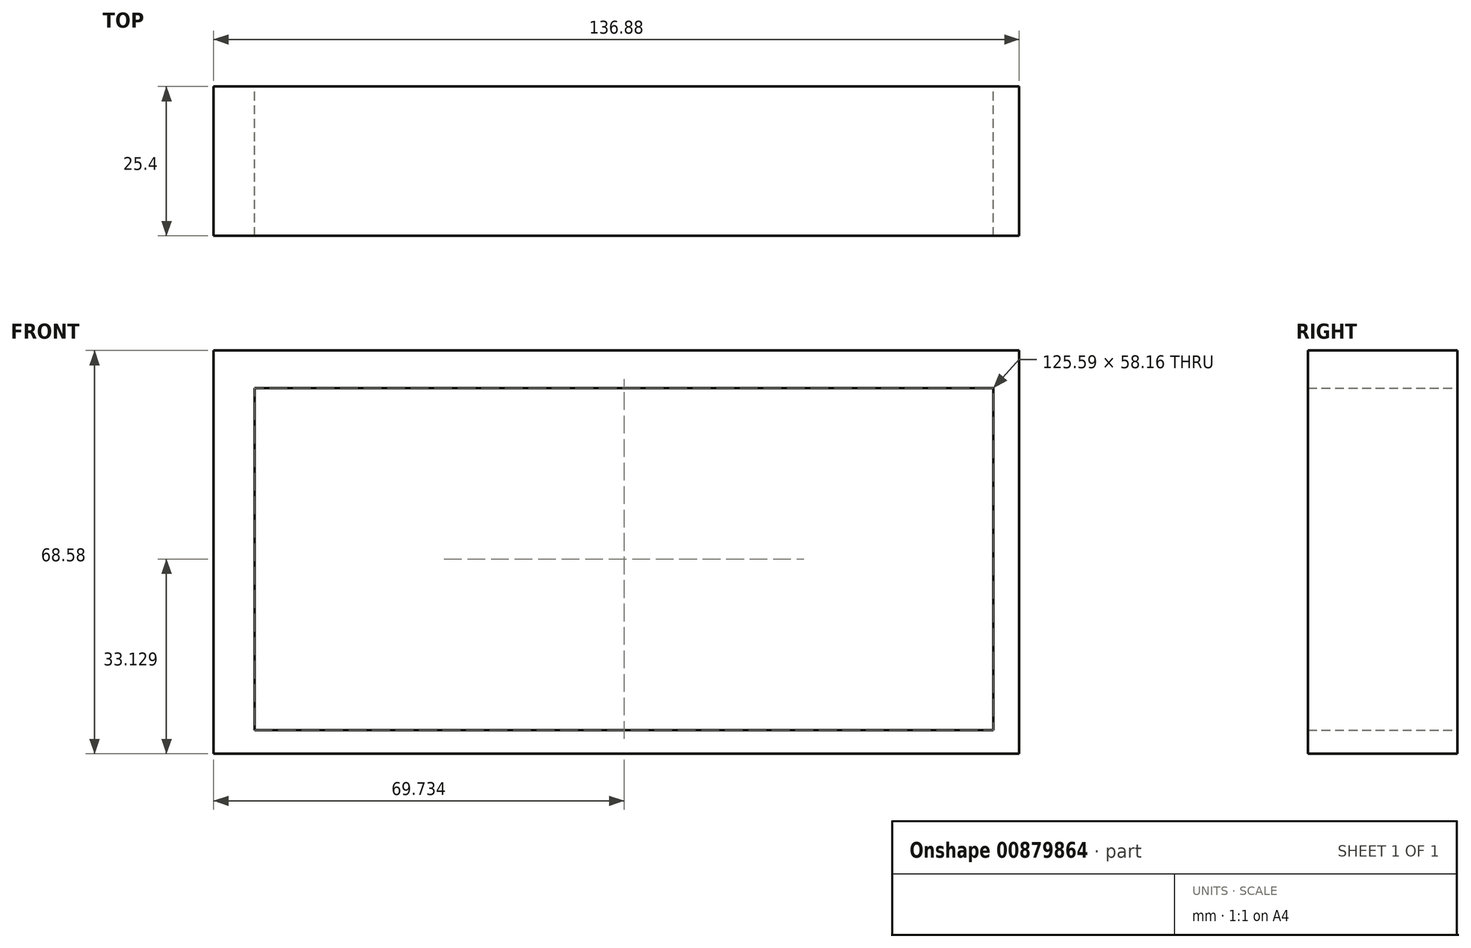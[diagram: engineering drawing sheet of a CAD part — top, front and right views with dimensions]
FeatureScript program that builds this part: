
annotation { "Feature Type Name" : "Feature", "Feature Type Description" : "" }
export const myFeature = defineFeature(function(context is Context, id is Id, definition is map)
    precondition{}
    {
        {
            var Q0;
            Q0=qCreatedBy(makeId("Front.planeOp"),FACE);
            var sketch = newSketch(context, id + "F0", { "sketchPlane" : qUnion([Q0])});
            skLineSegment(sketch, "E0", {"start": v(-51.07, 28.94) * mm, "end": v(85.8, 28.94) * mm});
            skLineSegment(sketch, "E1", {"start": v(85.8, 28.94) * mm, "end": v(85.8, -39.64) * mm});
            skLineSegment(sketch, "E2", {"start": v(85.8, -39.64) * mm, "end": v(-51.07, -39.64) * mm});
            skLineSegment(sketch, "E3", {"start": v(-51.07, -39.64) * mm, "end": v(-51.07, 28.94) * mm});
            skLineSegment(sketch, "E4", {"start": v(-44.13, 22.57) * mm, "end": v(-44.13, -35.6) * mm});
            skLineSegment(sketch, "E5", {"start": v(-44.13, -35.6) * mm, "end": v(81.46, -35.6) * mm});
            skLineSegment(sketch, "E6", {"start": v(81.46, -35.6) * mm, "end": v(81.46, 22.57) * mm});
            skLineSegment(sketch, "E7", {"start": v(81.46, 22.57) * mm, "end": v(-44.13, 22.57) * mm});
            skSolve(sketch);
        }
        {
            var Q0;
            Q0 = qSketchRegion(id + "F0", true);
            extrude(context, id + "F1", {"entities" : qUnion([Q0]), "depth" : 25.4 * mm, "offsetDistance" : 25.4 * mm});
        }
    });
